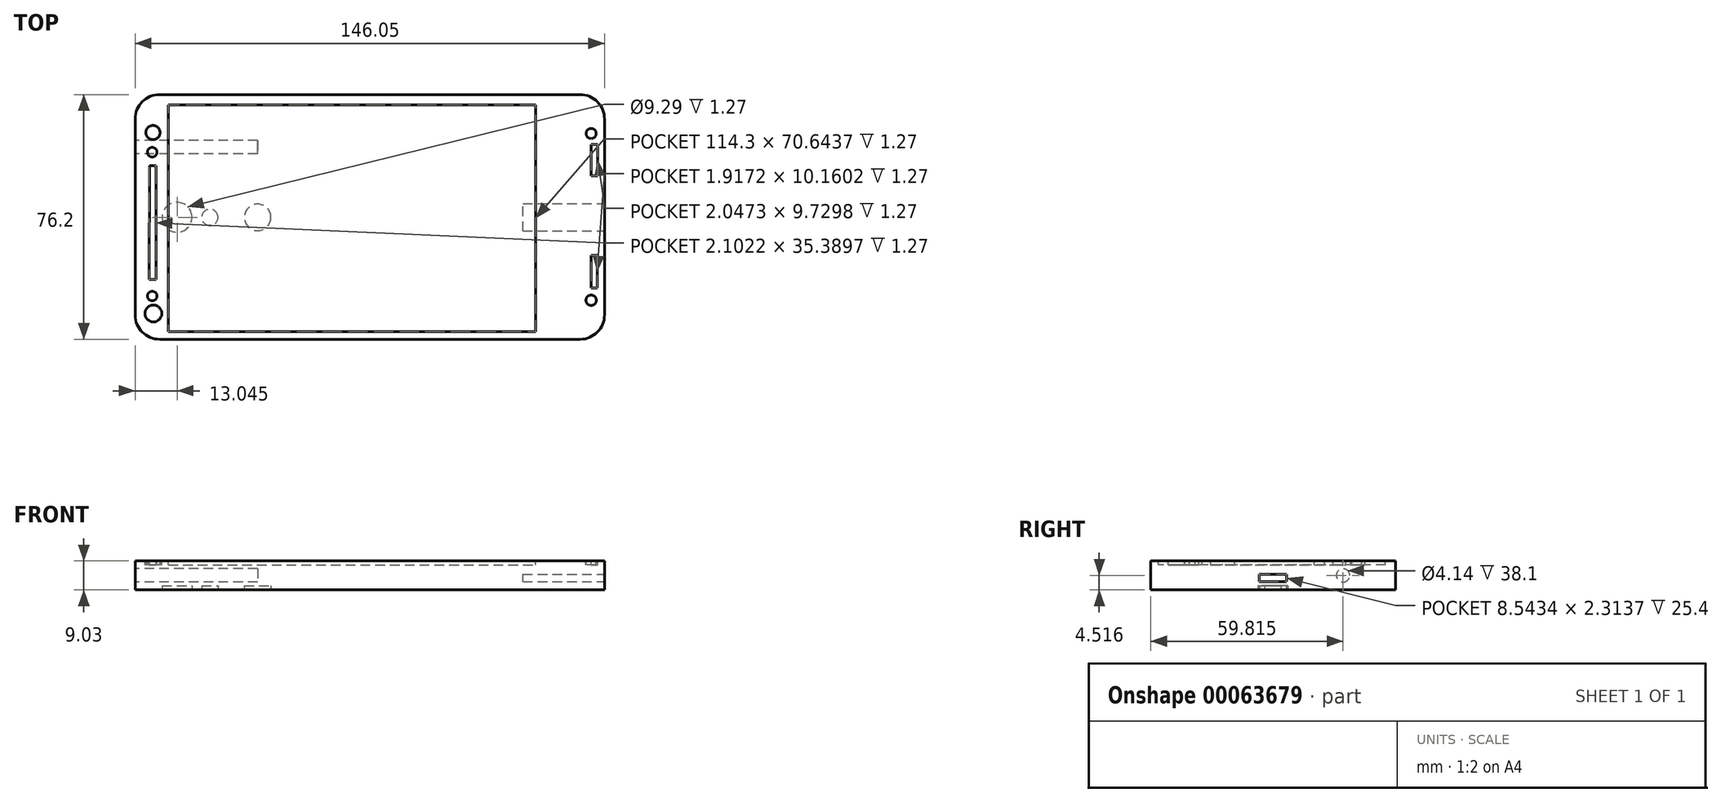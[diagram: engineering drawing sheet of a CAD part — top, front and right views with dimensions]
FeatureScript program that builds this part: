
annotation { "Feature Type Name" : "Feature", "Feature Type Description" : "" }
export const myFeature = defineFeature(function(context is Context, id is Id, definition is map)
    precondition{}
    {
        {
            var Q0;
            Q0=qCreatedBy(makeId("Top.planeOp"),FACE);
            var sketch = newSketch(context, id + "F0", { "sketchPlane" : qUnion([Q0])});
            skLineSegment(sketch, "E0.bottom", {"start": v(-70.09, 38.22) * mm, "end": v(75.96, 38.22) * mm});
            skLineSegment(sketch, "E0.top", {"start": v(-70.09, -37.98) * mm, "end": v(75.96, -37.98) * mm});
            skLineSegment(sketch, "E0.left", {"start": v(-70.09, 38.22) * mm, "end": v(-70.09, -37.98) * mm});
            skLineSegment(sketch, "E0.right", {"start": v(75.96, 38.22) * mm, "end": v(75.96, -37.98) * mm});
            skSolve(sketch);
        }
        {
            var Q0;
            Q0 = qSketchRegion(id + "F0", true);
            extrude(context, id + "F1", {"entities" : qUnion([Q0]), "depth" : 9.03 * mm});
        }
        {
            var Q0;
            Q0=makeQuery(id+"F1.opExtrude","SWEPT_EDGE",EDGE,{"disambiguationData":[OSD([sQuery(id+"F0.wireOp",EDGE,"E0.top"),sQuery(id+"F0.wireOp",EDGE,"E0.right")])]});
            var Q1;
            Q1=makeQuery(id+"F1.opExtrude","SWEPT_EDGE",EDGE,{"disambiguationData":[OSD([sQuery(id+"F0.wireOp",EDGE,"E0.top"),sQuery(id+"F0.wireOp",EDGE,"E0.left")])]});
            var Q2;
            Q2=makeQuery(id+"F1.opExtrude","SWEPT_EDGE",EDGE,{"disambiguationData":[OSD([sQuery(id+"F0.wireOp",EDGE,"E0.bottom"),sQuery(id+"F0.wireOp",EDGE,"E0.left")])]});
            var Q3;
            Q3=makeQuery(id+"F1.opExtrude","SWEPT_EDGE",EDGE,{"disambiguationData":[OSD([sQuery(id+"F0.wireOp",EDGE,"E0.bottom"),sQuery(id+"F0.wireOp",EDGE,"E0.right")])]});
            fillet(context, id + "F2", {"entities" : qUnion([Q0, Q1, Q2, Q3]), "radius" : 7.62 * mm, "tangentPropagation" : true, "allowEdgeOverflow" : false});
        }
        {
            var Q0;
            Q0=makeQuery(id+"F1.opExtrude","SWEPT_FACE",FACE,{"disambiguationData":[OSD([sQuery(id+"F0.wireOp",EDGE,"E0.right")])]});
            var sketch = newSketch(context, id + "F3", { "sketchPlane" : qUnion([Q0])});
            skPoint(sketch, "E1.endSnap0", {"position": v(-30.36, 4.52) * mm});
            skLineSegment(sketch, "E2", {"start": v(-4.27, 2.5) * mm, "end": v(4.27, 2.5) * mm});
            skLineSegment(sketch, "E3", {"start": v(-4.27, 2.5) * mm, "end": v(-4.27, 4.81) * mm});
            skLineSegment(sketch, "E4", {"start": v(4.27, 2.5) * mm, "end": v(4.27, 4.81) * mm});
            skPoint(sketch, "E5.centerSnap0", {"position": v(0, 2.5) * mm});
            skLineSegment(sketch, "E6", {"start": v(-4.27, 4.81) * mm, "end": v(4.27, 4.81) * mm});
            skSolve(sketch);
        }
        {
            var Q0;
            Q0 = qSketchRegion(id + "F3", true);
            extrude(context, id + "F4", {"entities" : qUnion([Q0]), "operationType" : NewBodyOperationType.REMOVE, "oppositeDirection" : true, "depth" : 25.4 * mm});
        }
        {
            var Q0;
            Q0=makeQuery(id+"F1.opExtrude","SWEPT_FACE",FACE,{"disambiguationData":[OSD([sQuery(id+"F0.wireOp",EDGE,"E0.left")])]});
            var sketch = newSketch(context, id + "F5", { "sketchPlane" : qUnion([Q0])});
            skCircle(sketch, "E7", {"center": v(-21.84, 4.52) * mm, "radius": 2.07 * mm});
            skPoint(sketch, "E7.centerSnap0", {"position": v(-30.6, 4.52) * mm});
            skSolve(sketch);
        }
        {
            var Q0;
            Q0 = qSketchRegion(id + "F5", true);
            extrude(context, id + "F6", {"entities" : qUnion([Q0]), "operationType" : NewBodyOperationType.REMOVE, "oppositeDirection" : true, "depth" : 2.54 * mm});
        }
        {
            var Q0;
            Q0 = qSketchRegion(id + "F5", true);
            extrude(context, id + "F7", {"entities" : qUnion([Q0]), "operationType" : NewBodyOperationType.REMOVE, "oppositeDirection" : true, "depth" : 38.1 * mm});
        }
        {
            var Q0;
            Q0=makeQuery(id+"F1.opExtrude","CAP_FACE",FACE,{"disambiguationData":[OSD([sQuery(id+"F0.wireOp",EDGE,"E0.bottom"),sQuery(id+"F0.wireOp",EDGE,"E0.top"),sQuery(id+"F0.wireOp",EDGE,"E0.left"),sQuery(id+"F0.wireOp",EDGE,"E0.right")])],"isStart":false});
            var sketch = newSketch(context, id + "F8", { "sketchPlane" : qUnion([Q0])});
            skLineSegment(sketch, "E8.bottom", {"start": v(-59.77, 35.04) * mm, "end": v(54.53, 35.04) * mm});
            skLineSegment(sketch, "E8.top", {"start": v(-59.77, -35.6) * mm, "end": v(54.53, -35.6) * mm});
            skLineSegment(sketch, "E8.left", {"start": v(-59.77, 35.04) * mm, "end": v(-59.77, -35.6) * mm});
            skLineSegment(sketch, "E8.right", {"start": v(54.53, 35.04) * mm, "end": v(54.53, -35.6) * mm});
            skSolve(sketch);
        }
        {
            var Q0;
            Q0 = qSketchRegion(id + "F8", true);
            extrude(context, id + "F9", {"entities" : qUnion([Q0]), "operationType" : NewBodyOperationType.REMOVE, "oppositeDirection" : true, "depth" : 1.27 * mm});
        }
        {
            var Q0;
            Q0=makeQuery(id+"F1.opExtrude","CAP_FACE",FACE,{"disambiguationData":[OSD([sQuery(id+"F0.wireOp",EDGE,"E0.bottom"),sQuery(id+"F0.wireOp",EDGE,"E0.top"),sQuery(id+"F0.wireOp",EDGE,"E0.left"),sQuery(id+"F0.wireOp",EDGE,"E0.right")])],"isStart":false});
            var sketch = newSketch(context, id + "F10", { "sketchPlane" : qUnion([Q0])});
            skCircle(sketch, "E9", {"center": v(-64.55, 26.4) * mm, "radius": 2.21 * mm});
            skCircle(sketch, "E10", {"center": v(-64.78, 20.28) * mm, "radius": 1.5 * mm});
            skCircle(sketch, "E11", {"center": v(71.8, 26.1) * mm, "radius": 1.57 * mm});
            skCircle(sketch, "E12", {"center": v(71.8, -25.83) * mm, "radius": 1.61 * mm});
            skCircle(sketch, "E13", {"center": v(-64.42, -29.95) * mm, "radius": 2.61 * mm});
            skCircle(sketch, "E14", {"center": v(-64.78, -24.52) * mm, "radius": 1.48 * mm});
            skLineSegment(sketch, "E15", {"start": v(-65.67, 16.05) * mm, "end": v(-63.61, 16.05) * mm});
            skLineSegment(sketch, "E16", {"start": v(-63.61, 16.05) * mm, "end": v(-63.61, -19.34) * mm});
            skLineSegment(sketch, "E17", {"start": v(-63.61, -19.34) * mm, "end": v(-65.71, -19.34) * mm});
            skLineSegment(sketch, "E18", {"start": v(-65.71, -19.34) * mm, "end": v(-65.67, 16.05) * mm});
            skLineSegment(sketch, "E19", {"start": v(71.8, 22.68) * mm, "end": v(73.85, 22.68) * mm});
            skLineSegment(sketch, "E20", {"start": v(73.85, 22.68) * mm, "end": v(73.85, 12.95) * mm});
            skLineSegment(sketch, "E21", {"start": v(73.85, 12.95) * mm, "end": v(71.8, 12.95) * mm});
            skLineSegment(sketch, "E22", {"start": v(71.8, 12.95) * mm, "end": v(71.8, 22.68) * mm});
            skLineSegment(sketch, "E23", {"start": v(71.8, -22.01) * mm, "end": v(73.72, -22.01) * mm});
            skLineSegment(sketch, "E24", {"start": v(73.72, -22.01) * mm, "end": v(73.72, -11.85) * mm});
            skLineSegment(sketch, "E25", {"start": v(73.72, -11.85) * mm, "end": v(71.8, -11.85) * mm});
            skLineSegment(sketch, "E26", {"start": v(71.8, -11.85) * mm, "end": v(71.8, -22.01) * mm});
            skSolve(sketch);
        }
        {
            var Q0;
            Q0 = qSketchRegion(id + "F10", true);
            extrude(context, id + "F11", {"entities" : qUnion([Q0]), "operationType" : NewBodyOperationType.REMOVE, "oppositeDirection" : true, "depth" : 1.27 * mm});
        }
        {
            var Q0;
            Q0=makeQuery(id+"F1.opExtrude","CAP_FACE",FACE,{"disambiguationData":[OSD([sQuery(id+"F0.wireOp",EDGE,"E0.bottom"),sQuery(id+"F0.wireOp",EDGE,"E0.top"),sQuery(id+"F0.wireOp",EDGE,"E0.left"),sQuery(id+"F0.wireOp",EDGE,"E0.right")])],"isStart":true});
            var sketch = newSketch(context, id + "F12", { "sketchPlane" : qUnion([Q0])});
            skCircle(sketch, "E27", {"center": v(-57.05, 0) * mm, "radius": 4.64 * mm});
            skCircle(sketch, "E28", {"center": v(-46.85, 0) * mm, "radius": 2.54 * mm});
            skCircle(sketch, "E29", {"center": v(-32, 0) * mm, "radius": 4.13 * mm});
            skSolve(sketch);
        }
        {
            var Q0;
            Q0 = qSketchRegion(id + "F12", true);
            extrude(context, id + "F13", {"entities" : qUnion([Q0]), "operationType" : NewBodyOperationType.REMOVE, "oppositeDirection" : true, "depth" : 1.27 * mm});
        }
    });
